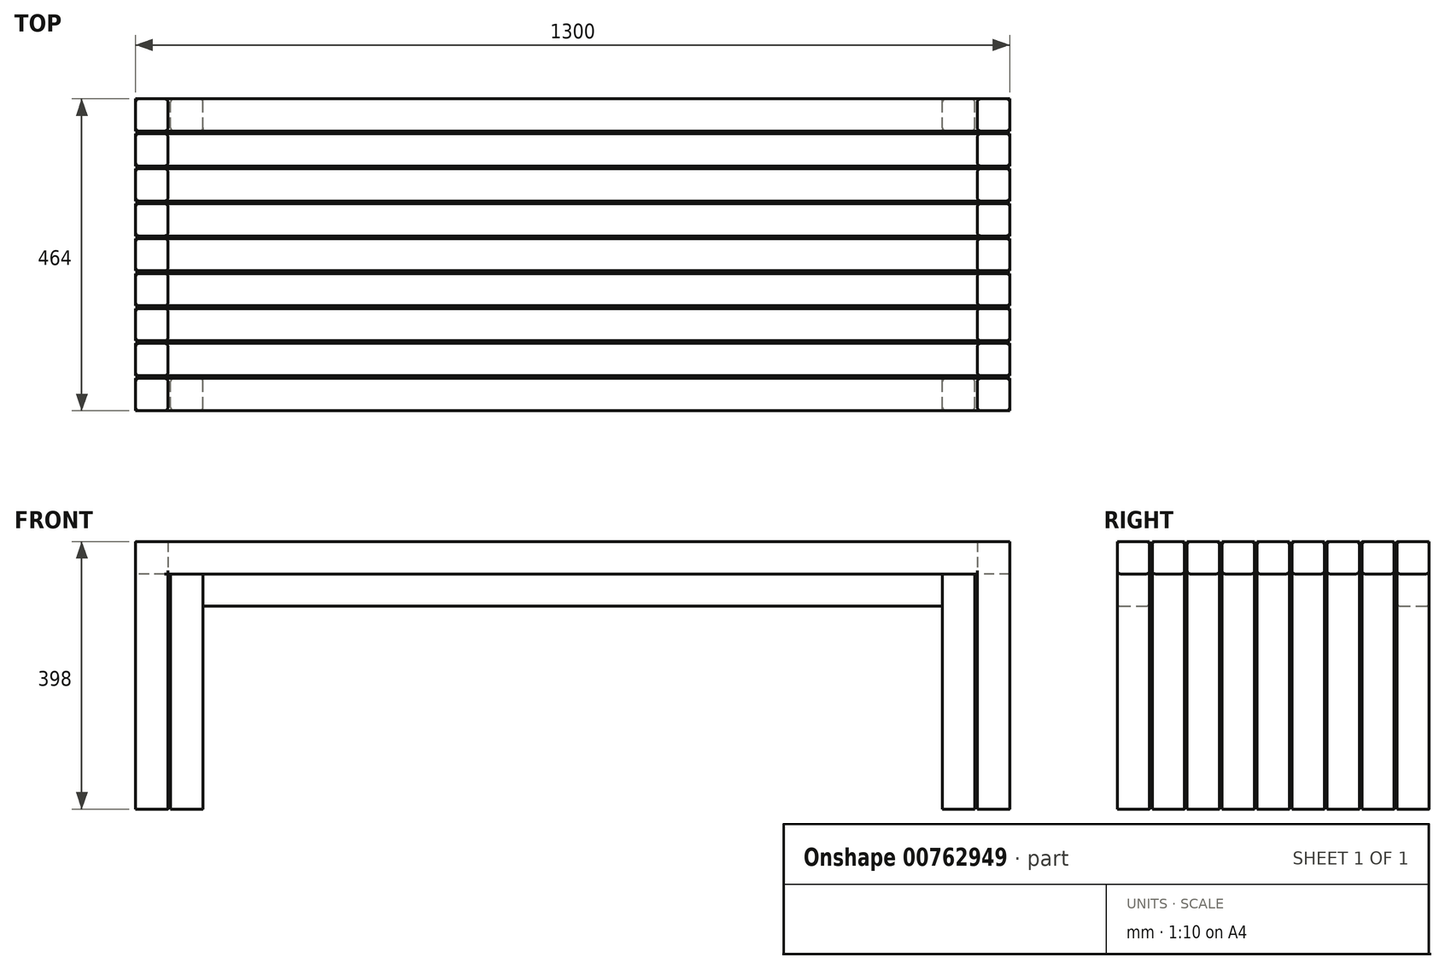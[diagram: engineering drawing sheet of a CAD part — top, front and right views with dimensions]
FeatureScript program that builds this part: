
annotation { "Feature Type Name" : "Feature", "Feature Type Description" : "" }
export const myFeature = defineFeature(function(context is Context, id is Id, definition is map)
    precondition{}
    {
        {
            var Q0;
            Q0=qCreatedBy(makeId("Right.planeOp"),FACE);
            var sketch = newSketch(context, id + "F0", { "sketchPlane" : qUnion([Q0])});
            skLineSegment(sketch, "E0.bottom", {"start": v(5, 0) * mm, "end": v(43, 0) * mm});
            skLineSegment(sketch, "E0.top", {"start": v(5, 48) * mm, "end": v(43, 48) * mm});
            skLineSegment(sketch, "E0.left", {"start": v(0, 5) * mm, "end": v(0, 43) * mm});
            skLineSegment(sketch, "E0.right", {"start": v(48, 5) * mm, "end": v(48, 43) * mm});
            skPoint(sketch, "E1.visualSharp", {"position": v(0, 48) * mm});
            skArc(sketch, "E1.filletArc", {"start": v(5, 48) * mm, "mid": v(1.46, 46.54) * mm, "end": v(0, 43) * mm});
            skPoint(sketch, "E2.visualSharp", {"position": v(48, 48) * mm});
            skArc(sketch, "E2.filletArc", {"start": v(48, 43) * mm, "mid": v(46.54, 46.54) * mm, "end": v(43, 48) * mm});
            skPoint(sketch, "E3.visualSharp", {"position": v(48, 0) * mm});
            skArc(sketch, "E3.filletArc", {"start": v(43, 0) * mm, "mid": v(46.54, 1.46) * mm, "end": v(48, 5) * mm});
            skPoint(sketch, "E4.visualSharp", {"position": v(0, 0) * mm});
            skArc(sketch, "E4.filletArc", {"start": v(0, 5) * mm, "mid": v(1.46, 1.46) * mm, "end": v(5, 0) * mm});
            skLineSegment(sketch, "E5.1.0.0", {"start": v(100, 5) * mm, "end": v(100, 43) * mm});
            skPoint(sketch, "E5.1.0.1", {"position": v(100, 48) * mm});
            skPoint(sketch, "E5.1.0.2", {"position": v(52, 48) * mm});
            skLineSegment(sketch, "E5.1.0.3", {"start": v(52, 5) * mm, "end": v(52, 43) * mm});
            skPoint(sketch, "E5.1.0.4", {"position": v(100, 0) * mm});
            skLineSegment(sketch, "E5.1.0.5", {"start": v(57, 48) * mm, "end": v(95, 48) * mm});
            skLineSegment(sketch, "E5.1.0.6", {"start": v(57, 0) * mm, "end": v(95, 0) * mm});
            skPoint(sketch, "E5.1.0.7", {"position": v(52, 0) * mm});
            skArc(sketch, "E5.1.0.8", {"start": v(57, 48) * mm, "mid": v(53.46, 46.54) * mm, "end": v(52, 43) * mm});
            skArc(sketch, "E5.1.0.9", {"start": v(100, 43) * mm, "mid": v(98.54, 46.54) * mm, "end": v(95, 48) * mm});
            skArc(sketch, "E5.1.0.10", {"start": v(95, 0) * mm, "mid": v(98.54, 1.46) * mm, "end": v(100, 5) * mm});
            skArc(sketch, "E5.1.0.11", {"start": v(52, 5) * mm, "mid": v(53.46, 1.46) * mm, "end": v(57, 0) * mm});
            skLineSegment(sketch, "E5.2.0.0", {"start": v(152, 5) * mm, "end": v(152, 43) * mm});
            skPoint(sketch, "E5.2.0.1", {"position": v(152, 48) * mm});
            skPoint(sketch, "E5.2.0.2", {"position": v(104, 48) * mm});
            skLineSegment(sketch, "E5.2.0.3", {"start": v(104, 5) * mm, "end": v(104, 43) * mm});
            skPoint(sketch, "E5.2.0.4", {"position": v(152, 0) * mm});
            skLineSegment(sketch, "E5.2.0.5", {"start": v(109, 48) * mm, "end": v(147, 48) * mm});
            skLineSegment(sketch, "E5.2.0.6", {"start": v(109, 0) * mm, "end": v(147, 0) * mm});
            skPoint(sketch, "E5.2.0.7", {"position": v(104, 0) * mm});
            skArc(sketch, "E5.2.0.8", {"start": v(109, 48) * mm, "mid": v(105.46, 46.54) * mm, "end": v(104, 43) * mm});
            skArc(sketch, "E5.2.0.9", {"start": v(152, 43) * mm, "mid": v(150.54, 46.54) * mm, "end": v(147, 48) * mm});
            skArc(sketch, "E5.2.0.10", {"start": v(147, 0) * mm, "mid": v(150.54, 1.46) * mm, "end": v(152, 5) * mm});
            skArc(sketch, "E5.2.0.11", {"start": v(104, 5) * mm, "mid": v(105.46, 1.46) * mm, "end": v(109, 0) * mm});
            skLineSegment(sketch, "E5.3.0.0", {"start": v(204, 5) * mm, "end": v(204, 43) * mm});
            skPoint(sketch, "E5.3.0.1", {"position": v(204, 48) * mm});
            skPoint(sketch, "E5.3.0.2", {"position": v(156, 48) * mm});
            skLineSegment(sketch, "E5.3.0.3", {"start": v(156, 5) * mm, "end": v(156, 43) * mm});
            skPoint(sketch, "E5.3.0.4", {"position": v(204, 0) * mm});
            skLineSegment(sketch, "E5.3.0.5", {"start": v(161, 48) * mm, "end": v(199, 48) * mm});
            skLineSegment(sketch, "E5.3.0.6", {"start": v(161, 0) * mm, "end": v(199, 0) * mm});
            skPoint(sketch, "E5.3.0.7", {"position": v(156, 0) * mm});
            skArc(sketch, "E5.3.0.8", {"start": v(161, 48) * mm, "mid": v(157.46, 46.54) * mm, "end": v(156, 43) * mm});
            skArc(sketch, "E5.3.0.9", {"start": v(204, 43) * mm, "mid": v(202.54, 46.54) * mm, "end": v(199, 48) * mm});
            skArc(sketch, "E5.3.0.10", {"start": v(199, 0) * mm, "mid": v(202.54, 1.46) * mm, "end": v(204, 5) * mm});
            skArc(sketch, "E5.3.0.11", {"start": v(156, 5) * mm, "mid": v(157.46, 1.46) * mm, "end": v(161, 0) * mm});
            skLineSegment(sketch, "E5.4.0.0", {"start": v(256, 5) * mm, "end": v(256, 43) * mm});
            skPoint(sketch, "E5.4.0.1", {"position": v(256, 48) * mm});
            skPoint(sketch, "E5.4.0.2", {"position": v(208, 48) * mm});
            skLineSegment(sketch, "E5.4.0.3", {"start": v(208, 5) * mm, "end": v(208, 43) * mm});
            skPoint(sketch, "E5.4.0.4", {"position": v(256, 0) * mm});
            skLineSegment(sketch, "E5.4.0.5", {"start": v(213, 48) * mm, "end": v(251, 48) * mm});
            skLineSegment(sketch, "E5.4.0.6", {"start": v(213, 0) * mm, "end": v(251, 0) * mm});
            skPoint(sketch, "E5.4.0.7", {"position": v(208, 0) * mm});
            skArc(sketch, "E5.4.0.8", {"start": v(213, 48) * mm, "mid": v(209.46, 46.54) * mm, "end": v(208, 43) * mm});
            skArc(sketch, "E5.4.0.9", {"start": v(256, 43) * mm, "mid": v(254.54, 46.54) * mm, "end": v(251, 48) * mm});
            skArc(sketch, "E5.4.0.10", {"start": v(251, 0) * mm, "mid": v(254.54, 1.46) * mm, "end": v(256, 5) * mm});
            skArc(sketch, "E5.4.0.11", {"start": v(208, 5) * mm, "mid": v(209.46, 1.46) * mm, "end": v(213, 0) * mm});
            skLineSegment(sketch, "E5.5.0.0", {"start": v(308, 5) * mm, "end": v(308, 43) * mm});
            skPoint(sketch, "E5.5.0.1", {"position": v(308, 48) * mm});
            skPoint(sketch, "E5.5.0.2", {"position": v(260, 48) * mm});
            skLineSegment(sketch, "E5.5.0.3", {"start": v(260, 5) * mm, "end": v(260, 43) * mm});
            skPoint(sketch, "E5.5.0.4", {"position": v(308, 0) * mm});
            skLineSegment(sketch, "E5.5.0.5", {"start": v(265, 48) * mm, "end": v(303, 48) * mm});
            skLineSegment(sketch, "E5.5.0.6", {"start": v(265, 0) * mm, "end": v(303, 0) * mm});
            skPoint(sketch, "E5.5.0.7", {"position": v(260, 0) * mm});
            skArc(sketch, "E5.5.0.8", {"start": v(265, 48) * mm, "mid": v(261.46, 46.54) * mm, "end": v(260, 43) * mm});
            skArc(sketch, "E5.5.0.9", {"start": v(308, 43) * mm, "mid": v(306.54, 46.54) * mm, "end": v(303, 48) * mm});
            skArc(sketch, "E5.5.0.10", {"start": v(303, 0) * mm, "mid": v(306.54, 1.46) * mm, "end": v(308, 5) * mm});
            skArc(sketch, "E5.5.0.11", {"start": v(260, 5) * mm, "mid": v(261.46, 1.46) * mm, "end": v(265, 0) * mm});
            skLineSegment(sketch, "E5.6.0.0", {"start": v(360, 5) * mm, "end": v(360, 43) * mm});
            skPoint(sketch, "E5.6.0.1", {"position": v(360, 48) * mm});
            skPoint(sketch, "E5.6.0.2", {"position": v(312, 48) * mm});
            skLineSegment(sketch, "E5.6.0.3", {"start": v(312, 5) * mm, "end": v(312, 43) * mm});
            skPoint(sketch, "E5.6.0.4", {"position": v(360, 0) * mm});
            skLineSegment(sketch, "E5.6.0.5", {"start": v(317, 48) * mm, "end": v(355, 48) * mm});
            skLineSegment(sketch, "E5.6.0.6", {"start": v(317, 0) * mm, "end": v(355, 0) * mm});
            skPoint(sketch, "E5.6.0.7", {"position": v(312, 0) * mm});
            skArc(sketch, "E5.6.0.8", {"start": v(317, 48) * mm, "mid": v(313.46, 46.54) * mm, "end": v(312, 43) * mm});
            skArc(sketch, "E5.6.0.9", {"start": v(360, 43) * mm, "mid": v(358.54, 46.54) * mm, "end": v(355, 48) * mm});
            skArc(sketch, "E5.6.0.10", {"start": v(355, 0) * mm, "mid": v(358.54, 1.46) * mm, "end": v(360, 5) * mm});
            skArc(sketch, "E5.6.0.11", {"start": v(312, 5) * mm, "mid": v(313.46, 1.46) * mm, "end": v(317, 0) * mm});
            skLineSegment(sketch, "E5.direction1", {"start": v(0, 0) * mm, "end": v(52, 0) * mm, "construction": true});
            skLineSegment(sketch, "E6.0.7.0", {"start": v(412, 5) * mm, "end": v(412, 43) * mm});
            skPoint(sketch, "E6.3.7.0", {"position": v(412, 48) * mm});
            skPoint(sketch, "E6.4.7.0", {"position": v(364, 48) * mm});
            skLineSegment(sketch, "E6.5.7.0", {"start": v(364, 5) * mm, "end": v(364, 43) * mm});
            skPoint(sketch, "E6.8.7.0", {"position": v(412, 0) * mm});
            skLineSegment(sketch, "E6.9.7.0", {"start": v(369, 48) * mm, "end": v(407, 48) * mm});
            skLineSegment(sketch, "E6.12.7.0", {"start": v(369, 0) * mm, "end": v(407, 0) * mm});
            skPoint(sketch, "E6.15.7.0", {"position": v(364, 0) * mm});
            skArc(sketch, "E6.16.7.0", {"start": v(369, 48) * mm, "mid": v(365.46, 46.54) * mm, "end": v(364, 43) * mm});
            skArc(sketch, "E6.20.7.0", {"start": v(412, 43) * mm, "mid": v(410.54, 46.54) * mm, "end": v(407, 48) * mm});
            skArc(sketch, "E6.24.7.0", {"start": v(407, 0) * mm, "mid": v(410.54, 1.46) * mm, "end": v(412, 5) * mm});
            skArc(sketch, "E6.28.7.0", {"start": v(364, 5) * mm, "mid": v(365.46, 1.46) * mm, "end": v(369, 0) * mm});
            skLineSegment(sketch, "E7.0.8.0", {"start": v(464, 5) * mm, "end": v(464, 43) * mm});
            skPoint(sketch, "E7.3.8.0", {"position": v(464, 48) * mm});
            skPoint(sketch, "E7.4.8.0", {"position": v(416, 48) * mm});
            skLineSegment(sketch, "E7.5.8.0", {"start": v(416, 5) * mm, "end": v(416, 43) * mm});
            skPoint(sketch, "E7.8.8.0", {"position": v(464, 0) * mm});
            skLineSegment(sketch, "E7.9.8.0", {"start": v(421, 48) * mm, "end": v(459, 48) * mm});
            skLineSegment(sketch, "E7.12.8.0", {"start": v(421, 0) * mm, "end": v(459, 0) * mm});
            skPoint(sketch, "E7.15.8.0", {"position": v(416, 0) * mm});
            skArc(sketch, "E7.16.8.0", {"start": v(421, 48) * mm, "mid": v(417.46, 46.54) * mm, "end": v(416, 43) * mm});
            skArc(sketch, "E7.20.8.0", {"start": v(464, 43) * mm, "mid": v(462.54, 46.54) * mm, "end": v(459, 48) * mm});
            skArc(sketch, "E7.24.8.0", {"start": v(459, 0) * mm, "mid": v(462.54, 1.46) * mm, "end": v(464, 5) * mm});
            skArc(sketch, "E7.28.8.0", {"start": v(416, 5) * mm, "mid": v(417.46, 1.46) * mm, "end": v(421, 0) * mm});
            skSolve(sketch);
        }
        {
            var Q0;
            Q0=makeQuery(id+"F0.imprint","IMPRINT",FACE,{"disambiguationData":[TD([[makeQuery(id+"F0.imprint","IMPRINT",EDGE,{"derivedFrom":sQuery(id+"F0.wireOp",EDGE,"E0.bottom")}),1.0]])]});
            var Q1;
            Q1=makeQuery(id+"F0.imprint","IMPRINT",FACE,{"disambiguationData":[TD([[makeQuery(id+"F0.imprint","IMPRINT",EDGE,{"derivedFrom":sQuery(id+"F0.wireOp",EDGE,"E5.1.0.0")}),1.0]])]});
            var Q2;
            Q2=makeQuery(id+"F0.imprint","IMPRINT",FACE,{"disambiguationData":[TD([[makeQuery(id+"F0.imprint","IMPRINT",EDGE,{"derivedFrom":sQuery(id+"F0.wireOp",EDGE,"E5.2.0.0")}),1.0]])]});
            var Q3;
            Q3=makeQuery(id+"F0.imprint","IMPRINT",FACE,{"disambiguationData":[TD([[makeQuery(id+"F0.imprint","IMPRINT",EDGE,{"derivedFrom":sQuery(id+"F0.wireOp",EDGE,"E5.3.0.0")}),1.0]])]});
            var Q4;
            Q4=makeQuery(id+"F0.imprint","IMPRINT",FACE,{"disambiguationData":[TD([[makeQuery(id+"F0.imprint","IMPRINT",EDGE,{"derivedFrom":sQuery(id+"F0.wireOp",EDGE,"E5.4.0.0")}),1.0]])]});
            var Q5;
            Q5=makeQuery(id+"F0.imprint","IMPRINT",FACE,{"disambiguationData":[TD([[makeQuery(id+"F0.imprint","IMPRINT",EDGE,{"derivedFrom":sQuery(id+"F0.wireOp",EDGE,"E5.5.0.0")}),1.0]])]});
            var Q6;
            Q6=makeQuery(id+"F0.imprint","IMPRINT",FACE,{"disambiguationData":[TD([[makeQuery(id+"F0.imprint","IMPRINT",EDGE,{"derivedFrom":sQuery(id+"F0.wireOp",EDGE,"E5.6.0.0")}),1.0]])]});
            var Q7;
            Q7=makeQuery(id+"F0.imprint","IMPRINT",FACE,{"disambiguationData":[TD([[makeQuery(id+"F0.imprint","IMPRINT",EDGE,{"derivedFrom":sQuery(id+"F0.wireOp",EDGE,"E6.0.7.0")}),1.0]])]});
            var Q8;
            Q8=makeQuery(id+"F0.imprint","IMPRINT",FACE,{"disambiguationData":[TD([[makeQuery(id+"F0.imprint","IMPRINT",EDGE,{"derivedFrom":sQuery(id+"F0.wireOp",EDGE,"E7.0.8.0")}),1.0]])]});
            extrude(context, id + "F1", {"entities" : qUnion([Q0, Q1, Q2, Q3, Q4, Q5, Q6, Q7, Q8]), "depth" : 1300 * mm, "offsetDistance" : 25 * mm});
        }
        {
            var Q0;
            Q0=qCreatedBy(makeId("Top.planeOp"),FACE);
            var sketch = newSketch(context, id + "F2", { "sketchPlane" : qUnion([Q0])});
            skLineSegment(sketch, "E8.bottom", {"start": v(5, 0) * mm, "end": v(43, 0) * mm});
            skLineSegment(sketch, "E8.top", {"start": v(5, 48) * mm, "end": v(43, 48) * mm});
            skLineSegment(sketch, "E8.left", {"start": v(0, 5) * mm, "end": v(0, 43) * mm});
            skLineSegment(sketch, "E8.right", {"start": v(48, 5) * mm, "end": v(48, 43) * mm});
            skPoint(sketch, "E9.visualSharp", {"position": v(48, 0) * mm});
            skArc(sketch, "E9.filletArc", {"start": v(43, 0) * mm, "mid": v(46.54, 1.46) * mm, "end": v(48, 5) * mm});
            skPoint(sketch, "E10.visualSharp", {"position": v(0, 0) * mm});
            skArc(sketch, "E10.filletArc", {"start": v(0, 5) * mm, "mid": v(1.46, 1.46) * mm, "end": v(5, 0) * mm});
            skPoint(sketch, "E11.visualSharp", {"position": v(0, 48) * mm});
            skArc(sketch, "E11.filletArc", {"start": v(5, 48) * mm, "mid": v(1.46, 46.54) * mm, "end": v(0, 43) * mm});
            skPoint(sketch, "E12.visualSharp", {"position": v(48, 48) * mm});
            skArc(sketch, "E12.filletArc", {"start": v(48, 43) * mm, "mid": v(46.54, 46.54) * mm, "end": v(43, 48) * mm});
            skPoint(sketch, "E13.0.1.0", {"position": v(48, 100) * mm});
            skPoint(sketch, "E13.0.1.1", {"position": v(0, 100) * mm});
            skPoint(sketch, "E13.0.1.2", {"position": v(0, 52) * mm});
            skPoint(sketch, "E13.0.1.3", {"position": v(48, 52) * mm});
            skLineSegment(sketch, "E13.0.1.4", {"start": v(5, 52) * mm, "end": v(43, 52) * mm});
            skLineSegment(sketch, "E13.0.1.5", {"start": v(5, 100) * mm, "end": v(43, 100) * mm});
            skLineSegment(sketch, "E13.0.1.6", {"start": v(0, 57) * mm, "end": v(0, 95) * mm});
            skLineSegment(sketch, "E13.0.1.7", {"start": v(48, 57) * mm, "end": v(48, 95) * mm});
            skArc(sketch, "E13.0.1.8", {"start": v(43, 52) * mm, "mid": v(46.54, 53.46) * mm, "end": v(48, 57) * mm});
            skArc(sketch, "E13.0.1.9", {"start": v(48, 95) * mm, "mid": v(46.54, 98.54) * mm, "end": v(43, 100) * mm});
            skArc(sketch, "E13.0.1.10", {"start": v(0, 57) * mm, "mid": v(1.46, 53.46) * mm, "end": v(5, 52) * mm});
            skArc(sketch, "E13.0.1.11", {"start": v(5, 100) * mm, "mid": v(1.46, 98.54) * mm, "end": v(0, 95) * mm});
            skPoint(sketch, "E13.0.2.0", {"position": v(48, 152) * mm});
            skPoint(sketch, "E13.0.2.1", {"position": v(0, 152) * mm});
            skPoint(sketch, "E13.0.2.2", {"position": v(0, 104) * mm});
            skPoint(sketch, "E13.0.2.3", {"position": v(48, 104) * mm});
            skLineSegment(sketch, "E13.0.2.4", {"start": v(5, 104) * mm, "end": v(43, 104) * mm});
            skLineSegment(sketch, "E13.0.2.5", {"start": v(5, 152) * mm, "end": v(43, 152) * mm});
            skLineSegment(sketch, "E13.0.2.6", {"start": v(0, 109) * mm, "end": v(0, 147) * mm});
            skLineSegment(sketch, "E13.0.2.7", {"start": v(48, 109) * mm, "end": v(48, 147) * mm});
            skArc(sketch, "E13.0.2.8", {"start": v(43, 104) * mm, "mid": v(46.54, 105.46) * mm, "end": v(48, 109) * mm});
            skArc(sketch, "E13.0.2.9", {"start": v(48, 147) * mm, "mid": v(46.54, 150.54) * mm, "end": v(43, 152) * mm});
            skArc(sketch, "E13.0.2.10", {"start": v(0, 109) * mm, "mid": v(1.46, 105.46) * mm, "end": v(5, 104) * mm});
            skArc(sketch, "E13.0.2.11", {"start": v(5, 152) * mm, "mid": v(1.46, 150.54) * mm, "end": v(0, 147) * mm});
            skPoint(sketch, "E13.0.3.0", {"position": v(48, 204) * mm});
            skPoint(sketch, "E13.0.3.1", {"position": v(0, 204) * mm});
            skPoint(sketch, "E13.0.3.2", {"position": v(0, 156) * mm});
            skPoint(sketch, "E13.0.3.3", {"position": v(48, 156) * mm});
            skLineSegment(sketch, "E13.0.3.4", {"start": v(5, 156) * mm, "end": v(43, 156) * mm});
            skLineSegment(sketch, "E13.0.3.5", {"start": v(5, 204) * mm, "end": v(43, 204) * mm});
            skLineSegment(sketch, "E13.0.3.6", {"start": v(0, 161) * mm, "end": v(0, 199) * mm});
            skLineSegment(sketch, "E13.0.3.7", {"start": v(48, 161) * mm, "end": v(48, 199) * mm});
            skArc(sketch, "E13.0.3.8", {"start": v(43, 156) * mm, "mid": v(46.54, 157.46) * mm, "end": v(48, 161) * mm});
            skArc(sketch, "E13.0.3.9", {"start": v(48, 199) * mm, "mid": v(46.54, 202.54) * mm, "end": v(43, 204) * mm});
            skArc(sketch, "E13.0.3.10", {"start": v(0, 161) * mm, "mid": v(1.46, 157.46) * mm, "end": v(5, 156) * mm});
            skArc(sketch, "E13.0.3.11", {"start": v(5, 204) * mm, "mid": v(1.46, 202.54) * mm, "end": v(0, 199) * mm});
            skPoint(sketch, "E13.0.4.0", {"position": v(48, 256) * mm});
            skPoint(sketch, "E13.0.4.1", {"position": v(0, 256) * mm});
            skPoint(sketch, "E13.0.4.2", {"position": v(0, 208) * mm});
            skPoint(sketch, "E13.0.4.3", {"position": v(48, 208) * mm});
            skLineSegment(sketch, "E13.0.4.4", {"start": v(5, 208) * mm, "end": v(43, 208) * mm});
            skLineSegment(sketch, "E13.0.4.5", {"start": v(5, 256) * mm, "end": v(43, 256) * mm});
            skLineSegment(sketch, "E13.0.4.6", {"start": v(0, 213) * mm, "end": v(0, 251) * mm});
            skLineSegment(sketch, "E13.0.4.7", {"start": v(48, 213) * mm, "end": v(48, 251) * mm});
            skArc(sketch, "E13.0.4.8", {"start": v(43, 208) * mm, "mid": v(46.54, 209.46) * mm, "end": v(48, 213) * mm});
            skArc(sketch, "E13.0.4.9", {"start": v(48, 251) * mm, "mid": v(46.54, 254.54) * mm, "end": v(43, 256) * mm});
            skArc(sketch, "E13.0.4.10", {"start": v(0, 213) * mm, "mid": v(1.46, 209.46) * mm, "end": v(5, 208) * mm});
            skArc(sketch, "E13.0.4.11", {"start": v(5, 256) * mm, "mid": v(1.46, 254.54) * mm, "end": v(0, 251) * mm});
            skPoint(sketch, "E13.0.5.0", {"position": v(48, 308) * mm});
            skPoint(sketch, "E13.0.5.1", {"position": v(0, 308) * mm});
            skPoint(sketch, "E13.0.5.2", {"position": v(0, 260) * mm});
            skPoint(sketch, "E13.0.5.3", {"position": v(48, 260) * mm});
            skLineSegment(sketch, "E13.0.5.4", {"start": v(5, 260) * mm, "end": v(43, 260) * mm});
            skLineSegment(sketch, "E13.0.5.5", {"start": v(5, 308) * mm, "end": v(43, 308) * mm});
            skLineSegment(sketch, "E13.0.5.6", {"start": v(0, 265) * mm, "end": v(0, 303) * mm});
            skLineSegment(sketch, "E13.0.5.7", {"start": v(48, 265) * mm, "end": v(48, 303) * mm});
            skArc(sketch, "E13.0.5.8", {"start": v(43, 260) * mm, "mid": v(46.54, 261.46) * mm, "end": v(48, 265) * mm});
            skArc(sketch, "E13.0.5.9", {"start": v(48, 303) * mm, "mid": v(46.54, 306.54) * mm, "end": v(43, 308) * mm});
            skArc(sketch, "E13.0.5.10", {"start": v(0, 265) * mm, "mid": v(1.46, 261.46) * mm, "end": v(5, 260) * mm});
            skArc(sketch, "E13.0.5.11", {"start": v(5, 308) * mm, "mid": v(1.46, 306.54) * mm, "end": v(0, 303) * mm});
            skPoint(sketch, "E13.0.6.0", {"position": v(48, 360) * mm});
            skPoint(sketch, "E13.0.6.1", {"position": v(0, 360) * mm});
            skPoint(sketch, "E13.0.6.2", {"position": v(0, 312) * mm});
            skPoint(sketch, "E13.0.6.3", {"position": v(48, 312) * mm});
            skLineSegment(sketch, "E13.0.6.4", {"start": v(5, 312) * mm, "end": v(43, 312) * mm});
            skLineSegment(sketch, "E13.0.6.5", {"start": v(5, 360) * mm, "end": v(43, 360) * mm});
            skLineSegment(sketch, "E13.0.6.6", {"start": v(0, 317) * mm, "end": v(0, 355) * mm});
            skLineSegment(sketch, "E13.0.6.7", {"start": v(48, 317) * mm, "end": v(48, 355) * mm});
            skArc(sketch, "E13.0.6.8", {"start": v(43, 312) * mm, "mid": v(46.54, 313.46) * mm, "end": v(48, 317) * mm});
            skArc(sketch, "E13.0.6.9", {"start": v(48, 355) * mm, "mid": v(46.54, 358.54) * mm, "end": v(43, 360) * mm});
            skArc(sketch, "E13.0.6.10", {"start": v(0, 317) * mm, "mid": v(1.46, 313.46) * mm, "end": v(5, 312) * mm});
            skArc(sketch, "E13.0.6.11", {"start": v(5, 360) * mm, "mid": v(1.46, 358.54) * mm, "end": v(0, 355) * mm});
            skPoint(sketch, "E13.0.7.0", {"position": v(48, 412) * mm});
            skPoint(sketch, "E13.0.7.1", {"position": v(0, 412) * mm});
            skPoint(sketch, "E13.0.7.2", {"position": v(0, 364) * mm});
            skPoint(sketch, "E13.0.7.3", {"position": v(48, 364) * mm});
            skLineSegment(sketch, "E13.0.7.4", {"start": v(5, 364) * mm, "end": v(43, 364) * mm});
            skLineSegment(sketch, "E13.0.7.5", {"start": v(5, 412) * mm, "end": v(43, 412) * mm});
            skLineSegment(sketch, "E13.0.7.6", {"start": v(0, 369) * mm, "end": v(0, 407) * mm});
            skLineSegment(sketch, "E13.0.7.7", {"start": v(48, 369) * mm, "end": v(48, 407) * mm});
            skArc(sketch, "E13.0.7.8", {"start": v(43, 364) * mm, "mid": v(46.54, 365.46) * mm, "end": v(48, 369) * mm});
            skArc(sketch, "E13.0.7.9", {"start": v(48, 407) * mm, "mid": v(46.54, 410.54) * mm, "end": v(43, 412) * mm});
            skArc(sketch, "E13.0.7.10", {"start": v(0, 369) * mm, "mid": v(1.46, 365.46) * mm, "end": v(5, 364) * mm});
            skArc(sketch, "E13.0.7.11", {"start": v(5, 412) * mm, "mid": v(1.46, 410.54) * mm, "end": v(0, 407) * mm});
            skPoint(sketch, "E13.0.8.0", {"position": v(48, 464) * mm});
            skPoint(sketch, "E13.0.8.1", {"position": v(0, 464) * mm});
            skPoint(sketch, "E13.0.8.2", {"position": v(0, 416) * mm});
            skPoint(sketch, "E13.0.8.3", {"position": v(48, 416) * mm});
            skLineSegment(sketch, "E13.0.8.4", {"start": v(5, 416) * mm, "end": v(43, 416) * mm});
            skLineSegment(sketch, "E13.0.8.5", {"start": v(5, 464) * mm, "end": v(43, 464) * mm});
            skLineSegment(sketch, "E13.0.8.6", {"start": v(0, 421) * mm, "end": v(0, 459) * mm});
            skLineSegment(sketch, "E13.0.8.7", {"start": v(48, 421) * mm, "end": v(48, 459) * mm});
            skArc(sketch, "E13.0.8.8", {"start": v(43, 416) * mm, "mid": v(46.54, 417.46) * mm, "end": v(48, 421) * mm});
            skArc(sketch, "E13.0.8.9", {"start": v(48, 459) * mm, "mid": v(46.54, 462.54) * mm, "end": v(43, 464) * mm});
            skArc(sketch, "E13.0.8.10", {"start": v(0, 421) * mm, "mid": v(1.46, 417.46) * mm, "end": v(5, 416) * mm});
            skArc(sketch, "E13.0.8.11", {"start": v(5, 464) * mm, "mid": v(1.46, 462.54) * mm, "end": v(0, 459) * mm});
            skPoint(sketch, "E13.1.0.0", {"position": v(1300, 48) * mm});
            skPoint(sketch, "E13.1.0.1", {"position": v(1252, 48) * mm});
            skPoint(sketch, "E13.1.0.2", {"position": v(1252, 0) * mm});
            skPoint(sketch, "E13.1.0.3", {"position": v(1300, 0) * mm});
            skLineSegment(sketch, "E13.1.0.4", {"start": v(1257, 0) * mm, "end": v(1295, 0) * mm});
            skLineSegment(sketch, "E13.1.0.5", {"start": v(1257, 48) * mm, "end": v(1295, 48) * mm});
            skLineSegment(sketch, "E13.1.0.6", {"start": v(1252, 5) * mm, "end": v(1252, 43) * mm});
            skLineSegment(sketch, "E13.1.0.7", {"start": v(1300, 5) * mm, "end": v(1300, 43) * mm});
            skArc(sketch, "E13.1.0.8", {"start": v(1295, 0) * mm, "mid": v(1298.54, 1.46) * mm, "end": v(1300, 5) * mm});
            skArc(sketch, "E13.1.0.9", {"start": v(1300, 43) * mm, "mid": v(1298.54, 46.54) * mm, "end": v(1295, 48) * mm});
            skArc(sketch, "E13.1.0.10", {"start": v(1252, 5) * mm, "mid": v(1253.46, 1.46) * mm, "end": v(1257, 0) * mm});
            skArc(sketch, "E13.1.0.11", {"start": v(1257, 48) * mm, "mid": v(1253.46, 46.54) * mm, "end": v(1252, 43) * mm});
            skPoint(sketch, "E13.1.1.0", {"position": v(1300, 100) * mm});
            skPoint(sketch, "E13.1.1.1", {"position": v(1252, 100) * mm});
            skPoint(sketch, "E13.1.1.2", {"position": v(1252, 52) * mm});
            skPoint(sketch, "E13.1.1.3", {"position": v(1300, 52) * mm});
            skLineSegment(sketch, "E13.1.1.4", {"start": v(1257, 52) * mm, "end": v(1295, 52) * mm});
            skLineSegment(sketch, "E13.1.1.5", {"start": v(1257, 100) * mm, "end": v(1295, 100) * mm});
            skLineSegment(sketch, "E13.1.1.6", {"start": v(1252, 57) * mm, "end": v(1252, 95) * mm});
            skLineSegment(sketch, "E13.1.1.7", {"start": v(1300, 57) * mm, "end": v(1300, 95) * mm});
            skArc(sketch, "E13.1.1.8", {"start": v(1295, 52) * mm, "mid": v(1298.54, 53.46) * mm, "end": v(1300, 57) * mm});
            skArc(sketch, "E13.1.1.9", {"start": v(1300, 95) * mm, "mid": v(1298.54, 98.54) * mm, "end": v(1295, 100) * mm});
            skArc(sketch, "E13.1.1.10", {"start": v(1252, 57) * mm, "mid": v(1253.46, 53.46) * mm, "end": v(1257, 52) * mm});
            skArc(sketch, "E13.1.1.11", {"start": v(1257, 100) * mm, "mid": v(1253.46, 98.54) * mm, "end": v(1252, 95) * mm});
            skPoint(sketch, "E13.1.2.0", {"position": v(1300, 152) * mm});
            skPoint(sketch, "E13.1.2.1", {"position": v(1252, 152) * mm});
            skPoint(sketch, "E13.1.2.2", {"position": v(1252, 104) * mm});
            skPoint(sketch, "E13.1.2.3", {"position": v(1300, 104) * mm});
            skLineSegment(sketch, "E13.1.2.4", {"start": v(1257, 104) * mm, "end": v(1295, 104) * mm});
            skLineSegment(sketch, "E13.1.2.5", {"start": v(1257, 152) * mm, "end": v(1295, 152) * mm});
            skLineSegment(sketch, "E13.1.2.6", {"start": v(1252, 109) * mm, "end": v(1252, 147) * mm});
            skLineSegment(sketch, "E13.1.2.7", {"start": v(1300, 109) * mm, "end": v(1300, 147) * mm});
            skArc(sketch, "E13.1.2.8", {"start": v(1295, 104) * mm, "mid": v(1298.54, 105.46) * mm, "end": v(1300, 109) * mm});
            skArc(sketch, "E13.1.2.9", {"start": v(1300, 147) * mm, "mid": v(1298.54, 150.54) * mm, "end": v(1295, 152) * mm});
            skArc(sketch, "E13.1.2.10", {"start": v(1252, 109) * mm, "mid": v(1253.46, 105.46) * mm, "end": v(1257, 104) * mm});
            skArc(sketch, "E13.1.2.11", {"start": v(1257, 152) * mm, "mid": v(1253.46, 150.54) * mm, "end": v(1252, 147) * mm});
            skPoint(sketch, "E13.1.3.0", {"position": v(1300, 204) * mm});
            skPoint(sketch, "E13.1.3.1", {"position": v(1252, 204) * mm});
            skPoint(sketch, "E13.1.3.2", {"position": v(1252, 156) * mm});
            skPoint(sketch, "E13.1.3.3", {"position": v(1300, 156) * mm});
            skLineSegment(sketch, "E13.1.3.4", {"start": v(1257, 156) * mm, "end": v(1295, 156) * mm});
            skLineSegment(sketch, "E13.1.3.5", {"start": v(1257, 204) * mm, "end": v(1295, 204) * mm});
            skLineSegment(sketch, "E13.1.3.6", {"start": v(1252, 161) * mm, "end": v(1252, 199) * mm});
            skLineSegment(sketch, "E13.1.3.7", {"start": v(1300, 161) * mm, "end": v(1300, 199) * mm});
            skArc(sketch, "E13.1.3.8", {"start": v(1295, 156) * mm, "mid": v(1298.54, 157.46) * mm, "end": v(1300, 161) * mm});
            skArc(sketch, "E13.1.3.9", {"start": v(1300, 199) * mm, "mid": v(1298.54, 202.54) * mm, "end": v(1295, 204) * mm});
            skArc(sketch, "E13.1.3.10", {"start": v(1252, 161) * mm, "mid": v(1253.46, 157.46) * mm, "end": v(1257, 156) * mm});
            skArc(sketch, "E13.1.3.11", {"start": v(1257, 204) * mm, "mid": v(1253.46, 202.54) * mm, "end": v(1252, 199) * mm});
            skPoint(sketch, "E13.1.4.0", {"position": v(1300, 256) * mm});
            skPoint(sketch, "E13.1.4.1", {"position": v(1252, 256) * mm});
            skPoint(sketch, "E13.1.4.2", {"position": v(1252, 208) * mm});
            skPoint(sketch, "E13.1.4.3", {"position": v(1300, 208) * mm});
            skLineSegment(sketch, "E13.1.4.4", {"start": v(1257, 208) * mm, "end": v(1295, 208) * mm});
            skLineSegment(sketch, "E13.1.4.5", {"start": v(1257, 256) * mm, "end": v(1295, 256) * mm});
            skLineSegment(sketch, "E13.1.4.6", {"start": v(1252, 213) * mm, "end": v(1252, 251) * mm});
            skLineSegment(sketch, "E13.1.4.7", {"start": v(1300, 213) * mm, "end": v(1300, 251) * mm});
            skArc(sketch, "E13.1.4.8", {"start": v(1295, 208) * mm, "mid": v(1298.54, 209.46) * mm, "end": v(1300, 213) * mm});
            skArc(sketch, "E13.1.4.9", {"start": v(1300, 251) * mm, "mid": v(1298.54, 254.54) * mm, "end": v(1295, 256) * mm});
            skArc(sketch, "E13.1.4.10", {"start": v(1252, 213) * mm, "mid": v(1253.46, 209.46) * mm, "end": v(1257, 208) * mm});
            skArc(sketch, "E13.1.4.11", {"start": v(1257, 256) * mm, "mid": v(1253.46, 254.54) * mm, "end": v(1252, 251) * mm});
            skPoint(sketch, "E13.1.5.0", {"position": v(1300, 308) * mm});
            skPoint(sketch, "E13.1.5.1", {"position": v(1252, 308) * mm});
            skPoint(sketch, "E13.1.5.2", {"position": v(1252, 260) * mm});
            skPoint(sketch, "E13.1.5.3", {"position": v(1300, 260) * mm});
            skLineSegment(sketch, "E13.1.5.4", {"start": v(1257, 260) * mm, "end": v(1295, 260) * mm});
            skLineSegment(sketch, "E13.1.5.5", {"start": v(1257, 308) * mm, "end": v(1295, 308) * mm});
            skLineSegment(sketch, "E13.1.5.6", {"start": v(1252, 265) * mm, "end": v(1252, 303) * mm});
            skLineSegment(sketch, "E13.1.5.7", {"start": v(1300, 265) * mm, "end": v(1300, 303) * mm});
            skArc(sketch, "E13.1.5.8", {"start": v(1295, 260) * mm, "mid": v(1298.54, 261.46) * mm, "end": v(1300, 265) * mm});
            skArc(sketch, "E13.1.5.9", {"start": v(1300, 303) * mm, "mid": v(1298.54, 306.54) * mm, "end": v(1295, 308) * mm});
            skArc(sketch, "E13.1.5.10", {"start": v(1252, 265) * mm, "mid": v(1253.46, 261.46) * mm, "end": v(1257, 260) * mm});
            skArc(sketch, "E13.1.5.11", {"start": v(1257, 308) * mm, "mid": v(1253.46, 306.54) * mm, "end": v(1252, 303) * mm});
            skPoint(sketch, "E13.1.6.0", {"position": v(1300, 360) * mm});
            skPoint(sketch, "E13.1.6.1", {"position": v(1252, 360) * mm});
            skPoint(sketch, "E13.1.6.2", {"position": v(1252, 312) * mm});
            skPoint(sketch, "E13.1.6.3", {"position": v(1300, 312) * mm});
            skLineSegment(sketch, "E13.1.6.4", {"start": v(1257, 312) * mm, "end": v(1295, 312) * mm});
            skLineSegment(sketch, "E13.1.6.5", {"start": v(1257, 360) * mm, "end": v(1295, 360) * mm});
            skLineSegment(sketch, "E13.1.6.6", {"start": v(1252, 317) * mm, "end": v(1252, 355) * mm});
            skLineSegment(sketch, "E13.1.6.7", {"start": v(1300, 317) * mm, "end": v(1300, 355) * mm});
            skArc(sketch, "E13.1.6.8", {"start": v(1295, 312) * mm, "mid": v(1298.54, 313.46) * mm, "end": v(1300, 317) * mm});
            skArc(sketch, "E13.1.6.9", {"start": v(1300, 355) * mm, "mid": v(1298.54, 358.54) * mm, "end": v(1295, 360) * mm});
            skArc(sketch, "E13.1.6.10", {"start": v(1252, 317) * mm, "mid": v(1253.46, 313.46) * mm, "end": v(1257, 312) * mm});
            skArc(sketch, "E13.1.6.11", {"start": v(1257, 360) * mm, "mid": v(1253.46, 358.54) * mm, "end": v(1252, 355) * mm});
            skPoint(sketch, "E13.1.7.0", {"position": v(1300, 412) * mm});
            skPoint(sketch, "E13.1.7.1", {"position": v(1252, 412) * mm});
            skPoint(sketch, "E13.1.7.2", {"position": v(1252, 364) * mm});
            skPoint(sketch, "E13.1.7.3", {"position": v(1300, 364) * mm});
            skLineSegment(sketch, "E13.1.7.4", {"start": v(1257, 364) * mm, "end": v(1295, 364) * mm});
            skLineSegment(sketch, "E13.1.7.5", {"start": v(1257, 412) * mm, "end": v(1295, 412) * mm});
            skLineSegment(sketch, "E13.1.7.6", {"start": v(1252, 369) * mm, "end": v(1252, 407) * mm});
            skLineSegment(sketch, "E13.1.7.7", {"start": v(1300, 369) * mm, "end": v(1300, 407) * mm});
            skArc(sketch, "E13.1.7.8", {"start": v(1295, 364) * mm, "mid": v(1298.54, 365.46) * mm, "end": v(1300, 369) * mm});
            skArc(sketch, "E13.1.7.9", {"start": v(1300, 407) * mm, "mid": v(1298.54, 410.54) * mm, "end": v(1295, 412) * mm});
            skArc(sketch, "E13.1.7.10", {"start": v(1252, 369) * mm, "mid": v(1253.46, 365.46) * mm, "end": v(1257, 364) * mm});
            skArc(sketch, "E13.1.7.11", {"start": v(1257, 412) * mm, "mid": v(1253.46, 410.54) * mm, "end": v(1252, 407) * mm});
            skPoint(sketch, "E13.1.8.0", {"position": v(1300, 464) * mm});
            skPoint(sketch, "E13.1.8.1", {"position": v(1252, 464) * mm});
            skPoint(sketch, "E13.1.8.2", {"position": v(1252, 416) * mm});
            skPoint(sketch, "E13.1.8.3", {"position": v(1300, 416) * mm});
            skLineSegment(sketch, "E13.1.8.4", {"start": v(1257, 416) * mm, "end": v(1295, 416) * mm});
            skLineSegment(sketch, "E13.1.8.5", {"start": v(1257, 464) * mm, "end": v(1295, 464) * mm});
            skLineSegment(sketch, "E13.1.8.6", {"start": v(1252, 421) * mm, "end": v(1252, 459) * mm});
            skLineSegment(sketch, "E13.1.8.7", {"start": v(1300, 421) * mm, "end": v(1300, 459) * mm});
            skArc(sketch, "E13.1.8.8", {"start": v(1295, 416) * mm, "mid": v(1298.54, 417.46) * mm, "end": v(1300, 421) * mm});
            skArc(sketch, "E13.1.8.9", {"start": v(1300, 459) * mm, "mid": v(1298.54, 462.54) * mm, "end": v(1295, 464) * mm});
            skArc(sketch, "E13.1.8.10", {"start": v(1252, 421) * mm, "mid": v(1253.46, 417.46) * mm, "end": v(1257, 416) * mm});
            skArc(sketch, "E13.1.8.11", {"start": v(1257, 464) * mm, "mid": v(1253.46, 462.54) * mm, "end": v(1252, 459) * mm});
            skLineSegment(sketch, "E13.direction1", {"start": v(0, 0) * mm, "end": v(1252, 0) * mm, "construction": true});
            skLineSegment(sketch, "E13.direction2", {"start": v(0, 0) * mm, "end": v(0, 52) * mm, "construction": true});
            skSolve(sketch);
        }
        {
            var Q0;
            Q0 = qSketchRegion(id + "F2", true);
            extrude(context, id + "F3", {"entities" : qUnion([Q0]), "depth" : 48 * mm, "offsetDistance" : 25 * mm, "hasSecondDirection" : true, "secondDirectionOppositeDirection" : true, "secondDirectionDepth" : 350 * mm});
        }
        {
            var Q0;
            Q0=qCreatedBy(makeId("Top.planeOp"),FACE);
            var sketch = newSketch(context, id + "F4", { "sketchPlane" : qUnion([Q0])});
            skLineSegment(sketch, "E14.bottom", {"start": v(57, 0) * mm, "end": v(95, 0) * mm});
            skLineSegment(sketch, "E14.top", {"start": v(57, 48) * mm, "end": v(95, 48) * mm});
            skLineSegment(sketch, "E14.left", {"start": v(52, 5) * mm, "end": v(52, 43) * mm});
            skLineSegment(sketch, "E14.right", {"start": v(100, 5) * mm, "end": v(100, 43) * mm});
            skPoint(sketch, "E15.visualSharp", {"position": v(100, 0) * mm});
            skArc(sketch, "E15.filletArc", {"start": v(95, 0) * mm, "mid": v(98.54, 1.46) * mm, "end": v(100, 5) * mm});
            skPoint(sketch, "E16.visualSharp", {"position": v(100, 48) * mm});
            skArc(sketch, "E16.filletArc", {"start": v(100, 43) * mm, "mid": v(98.54, 46.54) * mm, "end": v(95, 48) * mm});
            skPoint(sketch, "E17.visualSharp", {"position": v(52, 48) * mm});
            skArc(sketch, "E17.filletArc", {"start": v(57, 48) * mm, "mid": v(53.46, 46.54) * mm, "end": v(52, 43) * mm});
            skPoint(sketch, "E18.visualSharp", {"position": v(52, 0) * mm});
            skArc(sketch, "E18.filletArc", {"start": v(52, 5) * mm, "mid": v(53.46, 1.46) * mm, "end": v(57, 0) * mm});
            skLineSegment(sketch, "E19.0.1.0", {"start": v(57, 464) * mm, "end": v(95, 464) * mm});
            skLineSegment(sketch, "E19.0.1.1", {"start": v(52, 421) * mm, "end": v(52, 459) * mm});
            skPoint(sketch, "E19.0.1.2", {"position": v(100, 416) * mm});
            skLineSegment(sketch, "E19.0.1.3", {"start": v(100, 421) * mm, "end": v(100, 459) * mm});
            skLineSegment(sketch, "E19.0.1.4", {"start": v(57, 416) * mm, "end": v(95, 416) * mm});
            skPoint(sketch, "E19.0.1.5", {"position": v(100, 464) * mm});
            skPoint(sketch, "E19.0.1.6", {"position": v(52, 416) * mm});
            skPoint(sketch, "E19.0.1.7", {"position": v(52, 464) * mm});
            skArc(sketch, "E19.0.1.8", {"start": v(52, 421) * mm, "mid": v(53.46, 417.46) * mm, "end": v(57, 416) * mm});
            skArc(sketch, "E19.0.1.9", {"start": v(95, 416) * mm, "mid": v(98.54, 417.46) * mm, "end": v(100, 421) * mm});
            skArc(sketch, "E19.0.1.10", {"start": v(100, 459) * mm, "mid": v(98.54, 462.54) * mm, "end": v(95, 464) * mm});
            skArc(sketch, "E19.0.1.11", {"start": v(57, 464) * mm, "mid": v(53.46, 462.54) * mm, "end": v(52, 459) * mm});
            skLineSegment(sketch, "E19.1.0.0", {"start": v(1205, 48) * mm, "end": v(1243, 48) * mm});
            skLineSegment(sketch, "E19.1.0.1", {"start": v(1200, 5) * mm, "end": v(1200, 43) * mm});
            skPoint(sketch, "E19.1.0.2", {"position": v(1248, 0) * mm});
            skLineSegment(sketch, "E19.1.0.3", {"start": v(1248, 5) * mm, "end": v(1248, 43) * mm});
            skLineSegment(sketch, "E19.1.0.4", {"start": v(1205, 0) * mm, "end": v(1243, 0) * mm});
            skPoint(sketch, "E19.1.0.5", {"position": v(1248, 48) * mm});
            skPoint(sketch, "E19.1.0.6", {"position": v(1200, 0) * mm});
            skPoint(sketch, "E19.1.0.7", {"position": v(1200, 48) * mm});
            skArc(sketch, "E19.1.0.8", {"start": v(1200, 5) * mm, "mid": v(1201.46, 1.46) * mm, "end": v(1205, 0) * mm});
            skArc(sketch, "E19.1.0.9", {"start": v(1243, 0) * mm, "mid": v(1246.54, 1.46) * mm, "end": v(1248, 5) * mm});
            skArc(sketch, "E19.1.0.10", {"start": v(1248, 43) * mm, "mid": v(1246.54, 46.54) * mm, "end": v(1243, 48) * mm});
            skArc(sketch, "E19.1.0.11", {"start": v(1205, 48) * mm, "mid": v(1201.46, 46.54) * mm, "end": v(1200, 43) * mm});
            skLineSegment(sketch, "E19.1.1.0", {"start": v(1205, 464) * mm, "end": v(1243, 464) * mm});
            skLineSegment(sketch, "E19.1.1.1", {"start": v(1200, 421) * mm, "end": v(1200, 459) * mm});
            skPoint(sketch, "E19.1.1.2", {"position": v(1248, 416) * mm});
            skLineSegment(sketch, "E19.1.1.3", {"start": v(1248, 421) * mm, "end": v(1248, 459) * mm});
            skLineSegment(sketch, "E19.1.1.4", {"start": v(1205, 416) * mm, "end": v(1243, 416) * mm});
            skPoint(sketch, "E19.1.1.5", {"position": v(1248, 464) * mm});
            skPoint(sketch, "E19.1.1.6", {"position": v(1200, 416) * mm});
            skPoint(sketch, "E19.1.1.7", {"position": v(1200, 464) * mm});
            skArc(sketch, "E19.1.1.8", {"start": v(1200, 421) * mm, "mid": v(1201.46, 417.46) * mm, "end": v(1205, 416) * mm});
            skArc(sketch, "E19.1.1.9", {"start": v(1243, 416) * mm, "mid": v(1246.54, 417.46) * mm, "end": v(1248, 421) * mm});
            skArc(sketch, "E19.1.1.10", {"start": v(1248, 459) * mm, "mid": v(1246.54, 462.54) * mm, "end": v(1243, 464) * mm});
            skArc(sketch, "E19.1.1.11", {"start": v(1205, 464) * mm, "mid": v(1201.46, 462.54) * mm, "end": v(1200, 459) * mm});
            skLineSegment(sketch, "E19.direction1", {"start": v(52, 0) * mm, "end": v(1200, 0) * mm, "construction": true});
            skLineSegment(sketch, "E19.direction2", {"start": v(52, 0) * mm, "end": v(52, 416) * mm, "construction": true});
            skSolve(sketch);
        }
        {
            var Q0;
            Q0 = qSketchRegion(id + "F4", true);
            extrude(context, id + "F5", {"entities" : qUnion([Q0]), "oppositeDirection" : true, "depth" : 350 * mm, "offsetDistance" : 25 * mm});
        }
        {
            var Q0;
            Q0=makeQuery(id+"F5.opExtrude","SWEPT_FACE",FACE,{"disambiguationData":[OSD([sQuery(id+"F4.wireOp",EDGE,"E14.right")])]});
            cPlane(context, id + "F6", {"entities" : qUnion([Q0]), "cplaneType" : CPlaneType.OFFSET, "offset" : 0 * mm, "width" : 150 * mm, "height" : 150 * mm});
        }
        {
            var Q0;
            Q0=qCreatedBy(id+"F6.planeOp",FACE);
            var sketch = newSketch(context, id + "F7", { "sketchPlane" : qUnion([Q0])});
            skLineSegment(sketch, "E20.bottom", {"start": v(5, 0) * mm, "end": v(43, 0) * mm});
            skLineSegment(sketch, "E20.top", {"start": v(5, -48) * mm, "end": v(43, -48) * mm});
            skLineSegment(sketch, "E20.left", {"start": v(0, -5) * mm, "end": v(0, -43) * mm});
            skLineSegment(sketch, "E20.right", {"start": v(48, -5) * mm, "end": v(48, -43) * mm});
            skPoint(sketch, "E21.visualSharp", {"position": v(0, 0) * mm});
            skArc(sketch, "E21.filletArc", {"start": v(5, 0) * mm, "mid": v(1.46, -1.46) * mm, "end": v(0, -5) * mm});
            skPoint(sketch, "E22.visualSharp", {"position": v(0, -48) * mm});
            skArc(sketch, "E22.filletArc", {"start": v(0, -43) * mm, "mid": v(1.46, -46.54) * mm, "end": v(5, -48) * mm});
            skPoint(sketch, "E23.visualSharp", {"position": v(48, -48) * mm});
            skArc(sketch, "E23.filletArc", {"start": v(43, -48) * mm, "mid": v(46.54, -46.54) * mm, "end": v(48, -43) * mm});
            skPoint(sketch, "E24.visualSharp", {"position": v(48, 0) * mm});
            skArc(sketch, "E24.filletArc", {"start": v(48, -5) * mm, "mid": v(46.54, -1.46) * mm, "end": v(43, 0) * mm});
            skPoint(sketch, "E25.1.0.0", {"position": v(464, -48) * mm});
            skLineSegment(sketch, "E25.1.0.1", {"start": v(421, 0) * mm, "end": v(459, 0) * mm});
            skPoint(sketch, "E25.1.0.2", {"position": v(416, 0) * mm});
            skArc(sketch, "E25.1.0.3", {"start": v(421, 0) * mm, "mid": v(417.46, -1.46) * mm, "end": v(416, -5) * mm});
            skArc(sketch, "E25.1.0.4", {"start": v(459, -48) * mm, "mid": v(462.54, -46.54) * mm, "end": v(464, -43) * mm});
            skPoint(sketch, "E25.1.0.5", {"position": v(416, -48) * mm});
            skLineSegment(sketch, "E25.1.0.6", {"start": v(421, -48) * mm, "end": v(459, -48) * mm});
            skLineSegment(sketch, "E25.1.0.7", {"start": v(416, -5) * mm, "end": v(416, -43) * mm});
            skPoint(sketch, "E25.1.0.8", {"position": v(464, 0) * mm});
            skLineSegment(sketch, "E25.1.0.9", {"start": v(464, -5) * mm, "end": v(464, -43) * mm});
            skArc(sketch, "E25.1.0.10", {"start": v(416, -43) * mm, "mid": v(417.46, -46.54) * mm, "end": v(421, -48) * mm});
            skArc(sketch, "E25.1.0.11", {"start": v(464, -5) * mm, "mid": v(462.54, -1.46) * mm, "end": v(459, 0) * mm});
            skLineSegment(sketch, "E25.direction1", {"start": v(43, -48) * mm, "end": v(459, -48) * mm, "construction": true});
            skSolve(sketch);
        }
        {
            var Q0;
            Q0 = qSketchRegion(id + "F7", true);
            extrude(context, id + "F8", {"entities" : qUnion([Q0]), "depth" : 1100 * mm, "offsetDistance" : 25 * mm});
        }
    });
